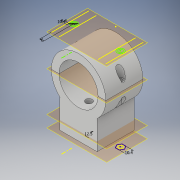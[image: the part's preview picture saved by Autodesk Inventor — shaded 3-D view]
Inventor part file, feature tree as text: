
AUTODESK INVENTOR PART (.ipt)
format: ipt  version: 2017 (Build 210142000, 142)  size: 230,912 bytes
history: native  units: mm
features: other x7, extrude x5, sketch x2, split x1, hole x1, imported_body x1
ambient origin geometry x8: Origin, YZ Plane, XZ Plane, XY Plane, X Axis, Y Axis, Z Axis, Center Point
bodies: Solid1 (feature_tree)
feature tree (17):
  extrude  "Extrusion1"  Depth=85.0mm
  other  "BoltPlane"
  other  "BoltHoles"
  extrude  "Extrusion2"  Depth=62.0mm
  extrude  "Extrusion3"  Depth=62.0mm TaperAngle=0.0deg
  other  "NutPlane"
  other  "NutHoles"
  extrude  "Extrusion4"  Depth=62.0mm
  other  "SplitPlane"
  split  "Split2"
  hole  "Hole2"  [1 undecoded]
  sketch  "Sketch4"  dims[d2=75.866mm d3=29.0mm d4=58.0mm d5=0.0mm d6=50.0mm d7=6.0mm d8=6.4mm d9=10.4mm d10=58.0mm d11=0.0mm d12=40.0mm d13=0.0mm d14=-80.0mm d15=10.4mm d16=70.0mm d17=0.0mm d18=0.0mm d28=12.5mm d29=6.2mm d30=6.0mm d31=4.0mm d32=2.0mm d33=90.0deg d34=8.0mm d35=0.0mm d36=10.2mm d37=10.2mm d38=18.0mm d39=62.0mm d40=0.0mm]
  other  "BoltHeadLevel"
  extrude  "Extrusion5"  Depth=62.0mm
  sketch  "Sketch1"  dims[d0=61.0mm d1=85.0mm]
  other  "UPPER"
  imported_body  "BASE"
note: 1 required parameter value undecoded (feature->parameter linkage not recoverable at this tier; creation-order binding heuristic only, values carry confidence <= 0.55)
